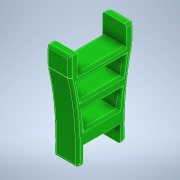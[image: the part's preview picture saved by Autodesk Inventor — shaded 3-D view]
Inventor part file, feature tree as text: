
AUTODESK INVENTOR PART (.ipt)
format: ipt  version: 2022 (Build 260153000, 153)  size: 210,944 bytes
history: native  units: in
note: dims shown in document units (in); Inventor stores cm internally (conversion verified against a paired STEP export)
features: sketch x2, extrude x1, fillet x1
ambient origin geometry x8: Origin, YZ Plane, XZ Plane, XY Plane, X Axis, Y Axis, Z Axis, Center Point
bodies: Body1 (feature_tree)
feature tree (4):
  extrude  "Extrusion2"  Depth=0.2469in
  sketch  "Sketch3"  dims[d8=1.3588in d9=0.7874in d10=0.0in d11=0.0787in]
  fillet  "Fillet2"  Radius=1.3588in
  sketch  "Sketch2"  dims[d5=0.2469in d6=0.2469in d7=1.3588in]
